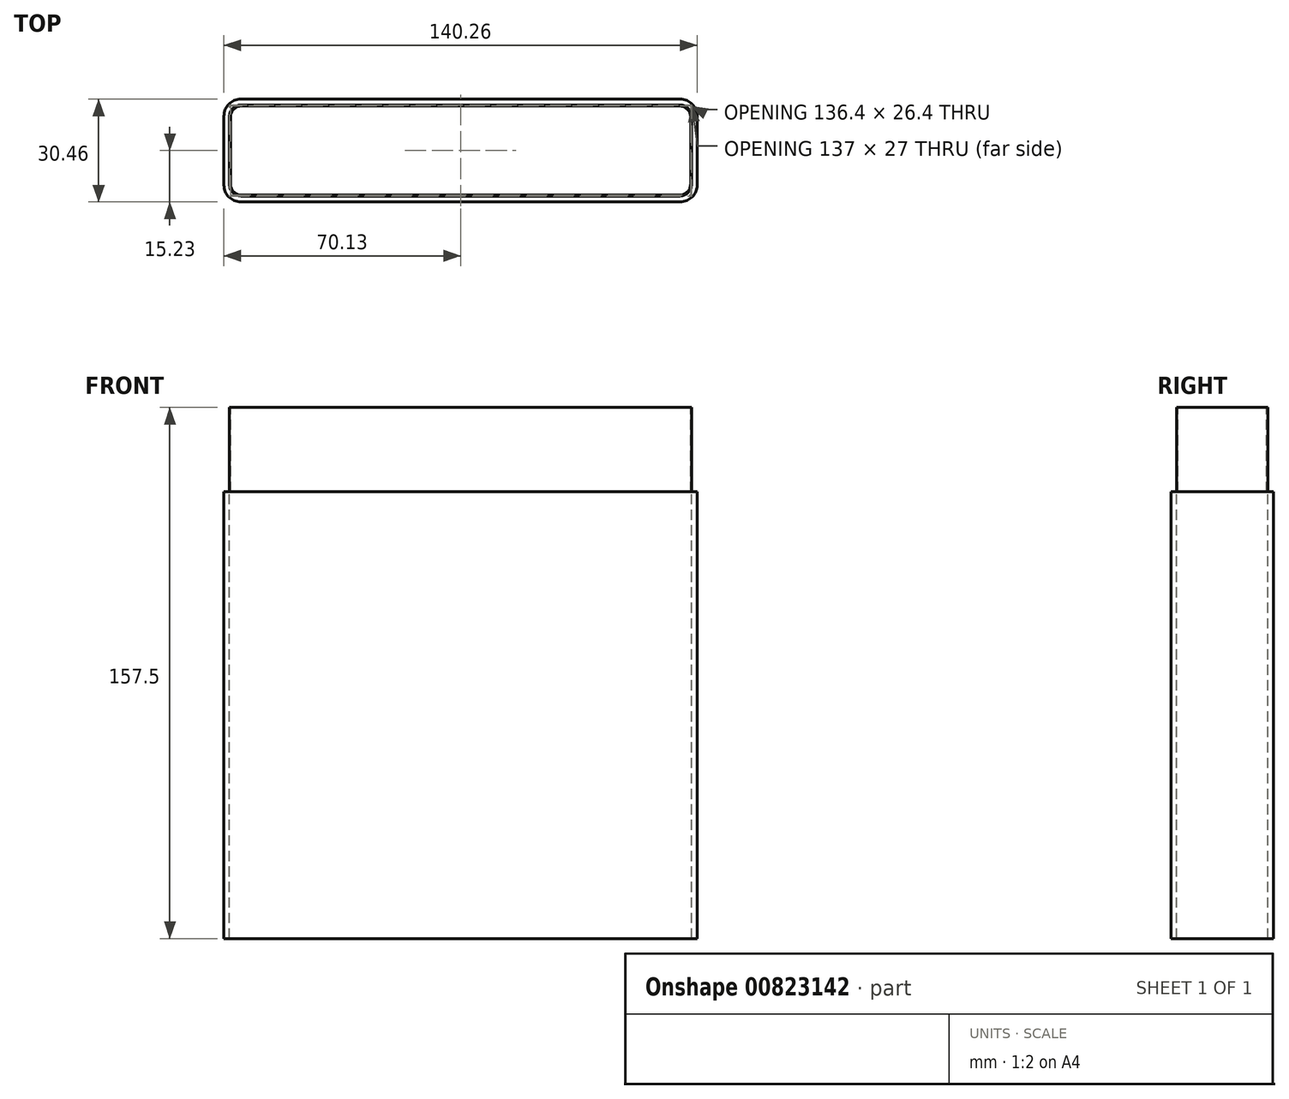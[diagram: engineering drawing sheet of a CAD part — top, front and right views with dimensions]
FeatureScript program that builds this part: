
annotation { "Feature Type Name" : "Feature", "Feature Type Description" : "" }
export const myFeature = defineFeature(function(context is Context, id is Id, definition is map)
    precondition{}
    {
        {
            var Q0;
            Q0=qCreatedBy(makeId("Top.planeOp"),FACE);
            var sketch = newSketch(context, id + "F0", { "sketchPlane" : qUnion([Q0])});
            skLineSegment(sketch, "E0.bottom", {"start": v(65.13, 15.23) * mm, "end": v(-65.13, 15.23) * mm});
            skLineSegment(sketch, "E0.top", {"start": v(65.13, -15.23) * mm, "end": v(-65.13, -15.23) * mm});
            skLineSegment(sketch, "E0.left", {"start": v(70.13, 10.23) * mm, "end": v(70.13, -10.23) * mm});
            skLineSegment(sketch, "E0.right", {"start": v(-70.13, 10.23) * mm, "end": v(-70.13, -10.23) * mm});
            skPoint(sketch, "E0.middle", {"position": v(0, 0) * mm});
            skPoint(sketch, "E1.visualSharp", {"position": v(-70.13, 15.23) * mm});
            skArc(sketch, "E1.filletArc", {"start": v(-65.13, 15.23) * mm, "mid": v(-68.67, 13.77) * mm, "end": v(-70.13, 10.23) * mm});
            skPoint(sketch, "E2.visualSharp", {"position": v(-70.13, -15.23) * mm});
            skArc(sketch, "E2.filletArc", {"start": v(-70.13, -10.23) * mm, "mid": v(-68.67, -13.77) * mm, "end": v(-65.13, -15.23) * mm});
            skPoint(sketch, "E3.visualSharp", {"position": v(70.13, -15.23) * mm});
            skArc(sketch, "E3.filletArc", {"start": v(65.13, -15.23) * mm, "mid": v(68.67, -13.77) * mm, "end": v(70.13, -10.23) * mm});
            skPoint(sketch, "E4.visualSharp", {"position": v(70.13, 15.23) * mm});
            skArc(sketch, "E4.filletArc", {"start": v(70.13, 10.23) * mm, "mid": v(68.67, 13.77) * mm, "end": v(65.13, 15.23) * mm});
            skSolve(sketch);
        }
        {
            var Q0;
            Q0=makeQuery(id+"F0.imprint","IMPRINT",FACE,{"disambiguationData":[TD([[makeQuery(id+"F0.imprint","IMPRINT",EDGE,{"derivedFrom":sQuery(id+"F0.wireOp",EDGE,"E0.bottom")}),1.0]])]});
            extrude(context, id + "F1", {"entities" : qUnion([Q0]), "depth" : 132.5 * mm, "offsetDistance" : 25 * mm});
        }
        {
            var Q0;
            Q0=makeQuery(id+"F1.opExtrude","CAP_FACE",FACE,{"disambiguationData":[OSD([sQuery(id+"F0.wireOp",EDGE,"E0.bottom"),sQuery(id+"F0.wireOp",EDGE,"E0.top"),sQuery(id+"F0.wireOp",EDGE,"E0.left"),sQuery(id+"F0.wireOp",EDGE,"E0.right"),sQuery(id+"F0.wireOp",EDGE,"E1.filletArc"),sQuery(id+"F0.wireOp",EDGE,"E2.filletArc"),sQuery(id+"F0.wireOp",EDGE,"E3.filletArc"),sQuery(id+"F0.wireOp",EDGE,"E4.filletArc")])],"isStart":false});
            var sketch = newSketch(context, id + "F2", { "sketchPlane" : qUnion([Q0])});
            skLineSegment(sketch, "E5.bottom", {"start": v(-65, 13.5) * mm, "end": v(65, 13.5) * mm});
            skLineSegment(sketch, "E5.top", {"start": v(-65, -13.5) * mm, "end": v(65, -13.5) * mm});
            skLineSegment(sketch, "E5.left", {"start": v(-68.5, 10) * mm, "end": v(-68.5, -10) * mm});
            skLineSegment(sketch, "E5.right", {"start": v(68.5, 10) * mm, "end": v(68.5, -10) * mm});
            skPoint(sketch, "E5.middle", {"position": v(0, 0) * mm});
            skPoint(sketch, "E6.visualSharp", {"position": v(-68.5, -13.5) * mm});
            skArc(sketch, "E6.filletArc", {"start": v(-68.5, -10) * mm, "mid": v(-67.47, -12.47) * mm, "end": v(-65, -13.5) * mm});
            skPoint(sketch, "E7.visualSharp", {"position": v(-68.5, 13.5) * mm});
            skArc(sketch, "E7.filletArc", {"start": v(-65, 13.5) * mm, "mid": v(-67.47, 12.47) * mm, "end": v(-68.5, 10) * mm});
            skPoint(sketch, "E8.visualSharp", {"position": v(68.5, -13.5) * mm});
            skArc(sketch, "E8.filletArc", {"start": v(65, -13.5) * mm, "mid": v(67.47, -12.47) * mm, "end": v(68.5, -10) * mm});
            skPoint(sketch, "E9.visualSharp", {"position": v(68.5, 13.5) * mm});
            skArc(sketch, "E9.filletArc", {"start": v(68.5, 10) * mm, "mid": v(67.47, 12.47) * mm, "end": v(65, 13.5) * mm});
            skSolve(sketch);
        }
        {
            var Q0;
            Q0=makeQuery(id+"F2.imprint","IMPRINT",FACE,{"disambiguationData":[TD([[makeQuery(id+"F2.imprint","IMPRINT",EDGE,{"derivedFrom":sQuery(id+"F2.wireOp",EDGE,"E5.bottom")}),-1.0]])]});
            extrude(context, id + "F3", {"entities" : qUnion([Q0]), "operationType" : NewBodyOperationType.REMOVE, "endBound" : BoundingType.UP_TO_NEXT, "oppositeDirection" : true, "depth" : 25 * mm, "offsetDistance" : 25 * mm});
        }
        {
            var Q0;
            Q0=makeQuery(id+"F2.imprint","IMPRINT",FACE,{"disambiguationData":[TD([[makeQuery(id+"F2.imprint","IMPRINT",EDGE,{"derivedFrom":sQuery(id+"F2.wireOp",EDGE,"E5.bottom")}),-1.0]])]});
            extrude(context, id + "F4", {"entities" : qUnion([Q0]), "depth" : 25 * mm, "offsetDistance" : 25 * mm});
        }
        {
            var Q0;
            Q0=makeQuery(id+"F4.opExtrude","CAP_FACE",FACE,{"disambiguationData":[OSD([sQuery(id+"F2.wireOp",EDGE,"E5.bottom"),sQuery(id+"F2.wireOp",EDGE,"E5.top"),sQuery(id+"F2.wireOp",EDGE,"E5.left"),sQuery(id+"F2.wireOp",EDGE,"E5.right"),sQuery(id+"F2.wireOp",EDGE,"E6.filletArc"),sQuery(id+"F2.wireOp",EDGE,"E7.filletArc"),sQuery(id+"F2.wireOp",EDGE,"E8.filletArc"),sQuery(id+"F2.wireOp",EDGE,"E9.filletArc")])],"isStart":false});
            var sketch = newSketch(context, id + "F5", { "sketchPlane" : qUnion([Q0])});
            skLineSegment(sketch, "E10.0", {"start": v(-68.2, 10) * mm, "end": v(-68.2, -10) * mm});
            skArc(sketch, "E10.1", {"start": v(-65, 13.2) * mm, "mid": v(-67.26, 12.26) * mm, "end": v(-68.2, 10) * mm});
            skArc(sketch, "E10.2", {"start": v(-68.2, -10) * mm, "mid": v(-67.26, -12.26) * mm, "end": v(-65, -13.2) * mm});
            skLineSegment(sketch, "E10.3", {"start": v(65, 13.2) * mm, "end": v(-65, 13.2) * mm});
            skLineSegment(sketch, "E10.4", {"start": v(-65, -13.2) * mm, "end": v(65, -13.2) * mm});
            skArc(sketch, "E10.5", {"start": v(65, -13.2) * mm, "mid": v(67.26, -12.26) * mm, "end": v(68.2, -10) * mm});
            skLineSegment(sketch, "E10.6", {"start": v(68.2, -10) * mm, "end": v(68.2, 10) * mm});
            skArc(sketch, "E10.7", {"start": v(68.2, 10) * mm, "mid": v(67.26, 12.26) * mm, "end": v(65, 13.2) * mm});
            skSolve(sketch);
        }
        {
            var Q0;
            Q0=makeQuery(id+"F5.imprint","IMPRINT",FACE,{"disambiguationData":[TD([[makeQuery(id+"F5.imprint","IMPRINT",EDGE,{"derivedFrom":sQuery(id+"F5.wireOp",EDGE,"E10.0")}),1.0]])]});
            extrude(context, id + "F6", {"entities" : qUnion([Q0]), "operationType" : NewBodyOperationType.REMOVE, "endBound" : BoundingType.UP_TO_NEXT, "oppositeDirection" : true, "depth" : 25 * mm, "offsetDistance" : 25 * mm});
        }
    });
